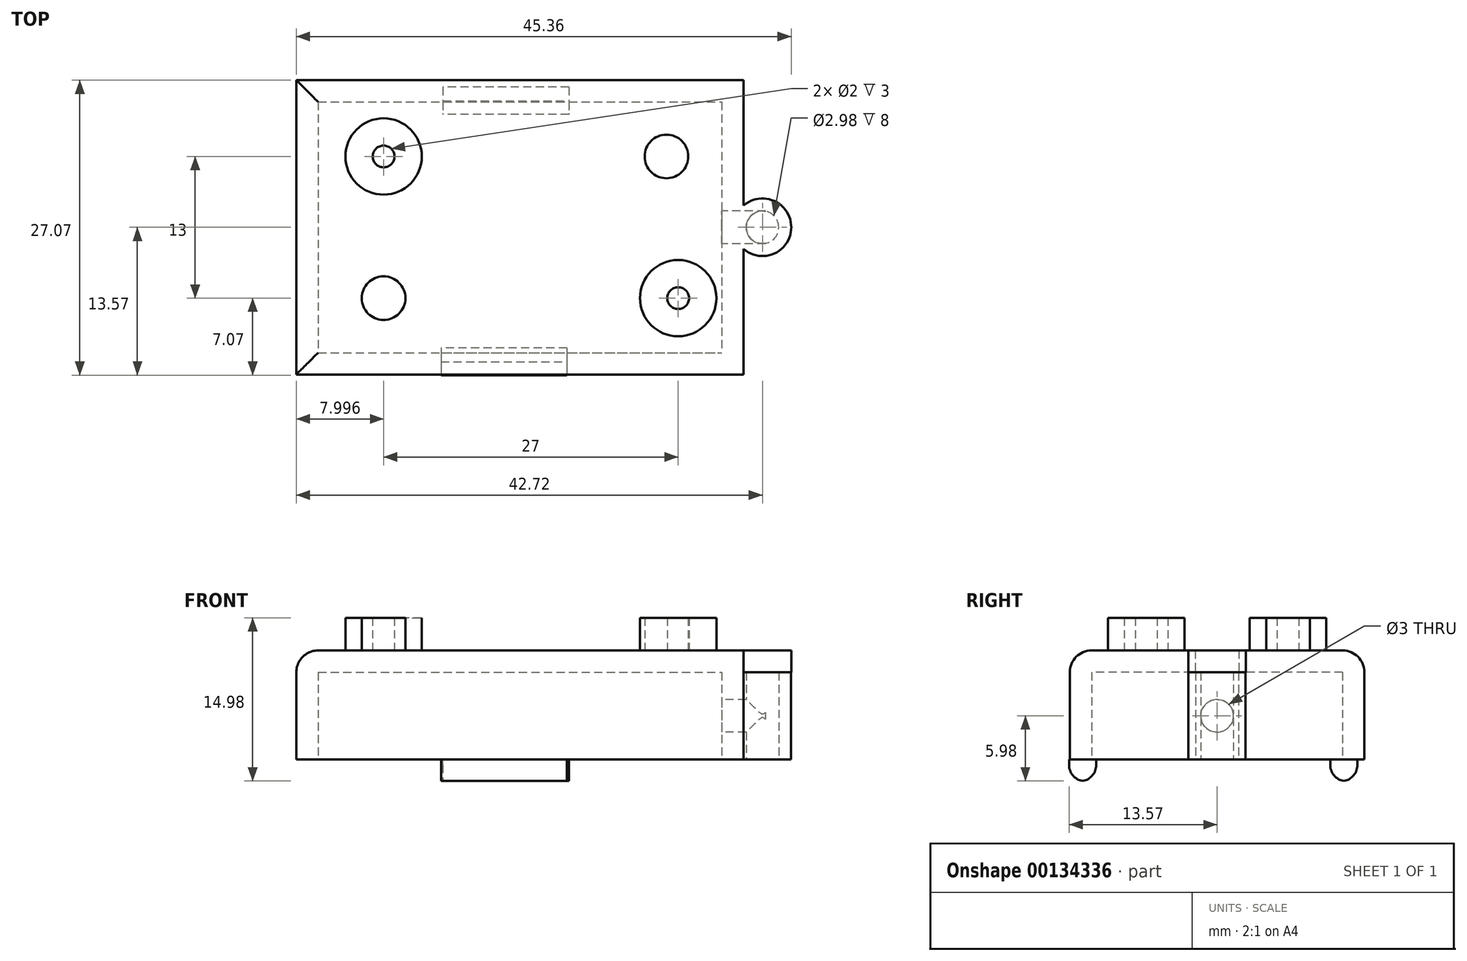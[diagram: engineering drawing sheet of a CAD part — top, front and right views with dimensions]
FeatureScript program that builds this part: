
annotation { "Feature Type Name" : "Feature", "Feature Type Description" : "" }
export const myFeature = defineFeature(function(context is Context, id is Id, definition is map)
    precondition{}
    {
        {
            var Q0;
            Q0=qCreatedBy(makeId("Top.planeOp"),FACE);
            var sketch = newSketch(context, id + "F0", { "sketchPlane" : qUnion([Q0])});
            skLineSegment(sketch, "E0.bottom", {"start": v(-49.4, 25) * mm, "end": v(-12.4, 25) * mm});
            skLineSegment(sketch, "E0.top", {"start": v(-49.4, 2) * mm, "end": v(-12.4, 2) * mm});
            skLineSegment(sketch, "E0.left", {"start": v(-49.4, 25) * mm, "end": v(-49.4, 2) * mm});
            skLineSegment(sketch, "E0.right", {"start": v(-12.4, 25) * mm, "end": v(-12.4, 2) * mm});
            skLineSegment(sketch, "E1.bottom", {"start": v(-51.4, 27) * mm, "end": v(-10.4, 27) * mm});
            skLineSegment(sketch, "E1.top", {"start": v(-51.4, 0) * mm, "end": v(-10.4, 0) * mm});
            skLineSegment(sketch, "E1.left", {"start": v(-51.4, 27) * mm, "end": v(-51.4, 0) * mm});
            skLineSegment(sketch, "E1.right", {"start": v(-10.4, 27) * mm, "end": v(-10.4, 0) * mm});
            skCircle(sketch, "E2", {"center": v(-8.68, 13.5) * mm, "radius": 1.5 * mm});
            skPoint(sketch, "E2.centerSnap0", {"position": v(-10.4, 13.5) * mm});
            skCircle(sketch, "E3", {"center": v(-8.68, 13.5) * mm, "radius": 2.62 * mm});
            skSolve(sketch);
        }
        {
            var Q0;
            Q0=makeQuery(id+"F0.imprint","IMPRINT",FACE,{"disambiguationData":[TD([[makeQuery(id+"F0.imprint","IMPRINT",EDGE,{"derivedFrom":sQuery(id+"F0.wireOp",EDGE,"E0.bottom")}),1.0]])]});
            var Q1;
            Q1=makeQuery(id+"F0.imprint","IMPRINT",FACE,{"disambiguationData":[TD([[makeQuery(id+"F0.imprint","IMPRINT",EDGE,{"derivedFrom":sQuery(id+"F0.wireOp",EDGE,"E2")}),-1.0]])]});
            var Q2;
            {var subQ0=sQuery(id+"F0.wireOp",EDGE,"E3");var subQ1=sQuery(id+"F0.wireOp",EDGE,"E1.right");var subQ2=makeQuery(id+"F0.imprint","INTERSECT",VERTEX,{"disambiguationData":[OD(0.0)],"derivedFrom":[subQ1,subQ0]});Q2=makeQuery(id+"F0.imprint","IMPRINT",FACE,{"disambiguationData":[TD([[makeQuery(id+"F0.imprint","IMPRINT",EDGE,{"disambiguationData":[TD([[subQ2,-1.0]])],"derivedFrom":subQ1}),-1.0]])]});}
            var Q3;
            Q3=sQuery(id+"F0.wireOp",EDGE,"E1.top");
            var Q4;
            Q4=sQuery(id+"F0.wireOp",EDGE,"E1.bottom");
            var Q5;
            Q5=sQuery(id+"F0.wireOp",EDGE,"E0.bottom");
            var Q6;
            Q6=sQuery(id+"F0.wireOp",EDGE,"E1.left");
            var Q7;
            Q7=sQuery(id+"F0.wireOp",EDGE,"E0.left");
            var Q8;
            Q8=sQuery(id+"F0.wireOp",EDGE,"E0.top");
            var Q9;
            Q9=sQuery(id+"F0.wireOp",EDGE,"E0.right");
            var Q10;
            Q10=sQuery(id+"F0.wireOp",EDGE,"E1.right");
            var Q11;
            Q11=sQuery(id+"F0.wireOp",EDGE,"E2");
            var Q12;
            Q12=sQuery(id+"F0.wireOp",EDGE,"E3");
            extrude(context, id + "F1", {"entities" : qUnion([Q0, Q1, Q2]), "surfaceEntities" : qUnion([Q3, Q4, Q5, Q6, Q7, Q8, Q9, Q10, Q11, Q12]), "depth" : 8 * mm});
        }
        {
            var Q0;
            Q0=makeQuery(id+"F1.opExtrude","SWEPT_FACE",FACE,{"disambiguationData":[OSD([sQuery(id+"F0.wireOp",EDGE,"E0.right")])]});
            var sketch = newSketch(context, id + "F2", { "sketchPlane" : qUnion([Q0])});
            skPoint(sketch, "E4", {"position": v(-13.5, 4) * mm});
            skPoint(sketch, "E4.positionSnap0", {"position": v(-13.5, 8) * mm});
            skSolve(sketch);
        }
        {
            var Q0;
            Q0=sQuery(id+"F2.wireOp",VERTEX,"E4");
            var Q1;
            Q1=makeQuery(id+"F1.opExtrude","SWEPT_BODY",BODY,{"disambiguationData":[OSD([sQuery(id+"F0.wireOp",EDGE,"E0.bottom"),sQuery(id+"F0.wireOp",EDGE,"E0.top"),sQuery(id+"F0.wireOp",EDGE,"E0.left"),sQuery(id+"F0.wireOp",EDGE,"E0.right"),sQuery(id+"F0.wireOp",EDGE,"E1.bottom"),sQuery(id+"F0.wireOp",EDGE,"E1.top"),sQuery(id+"F0.wireOp",EDGE,"E1.left"),sQuery(id+"F0.wireOp",EDGE,"E1.right"),sQuery(id+"F0.wireOp",EDGE,"E2"),sQuery(id+"F0.wireOp",EDGE,"E3")])]});
            hole(context, id + "F3", {"style" : HoleStyle.SIMPLE, "endStyle" : HoleEndStyle.BLIND, "holeDiameter" : 3 * mm, "holeDepth" : 4 * mm, "locations" : qUnion([Q0]), "scope" : qUnion([Q1])});
        }
        {
            var Q0;
            Q0=makeQuery(id+"F1.opExtrude","CAP_FACE",FACE,{"disambiguationData":[OSD([sQuery(id+"F0.wireOp",EDGE,"E0.bottom"),sQuery(id+"F0.wireOp",EDGE,"E0.top"),sQuery(id+"F0.wireOp",EDGE,"E0.left"),sQuery(id+"F0.wireOp",EDGE,"E0.right"),sQuery(id+"F0.wireOp",EDGE,"E1.bottom"),sQuery(id+"F0.wireOp",EDGE,"E1.top"),sQuery(id+"F0.wireOp",EDGE,"E1.left"),sQuery(id+"F0.wireOp",EDGE,"E1.right"),sQuery(id+"F0.wireOp",EDGE,"E2"),sQuery(id+"F0.wireOp",EDGE,"E3")])],"isStart":false});
            var sketch = newSketch(context, id + "F4", { "sketchPlane" : qUnion([Q0])});
            skLineSegment(sketch, "E5.bottom", {"start": v(-51.4, 27) * mm, "end": v(-10.4, 27) * mm});
            skLineSegment(sketch, "E5.top", {"start": v(-51.4, 0) * mm, "end": v(-10.4, 0) * mm});
            skLineSegment(sketch, "E5.left", {"start": v(-51.4, 27) * mm, "end": v(-51.4, 0) * mm});
            skLineSegment(sketch, "E5.right", {"start": v(-10.4, 27) * mm, "end": v(-10.4, 0) * mm});
            skCircle(sketch, "E6", {"center": v(-8.68, 13.5) * mm, "radius": 2.64 * mm});
            skSolve(sketch);
        }
        {
            var Q0;
            Q0 = qSketchRegion(id + "F4", true);
            extrude(context, id + "F5", {"entities" : qUnion([Q0]), "operationType" : NewBodyOperationType.ADD, "depth" : 2 * mm});
        }
        {
            var Q0;
            Q0=makeQuery(id+"F5.opExtrude","CAP_EDGE",EDGE,{"disambiguationData":[OSD([sQuery(id+"F4.wireOp",EDGE,"E5.left")])],"isStart":false});
            var Q1;
            Q1=makeQuery(id+"F5.opExtrude","CAP_EDGE",EDGE,{"disambiguationData":[OSD([sQuery(id+"F4.wireOp",EDGE,"E5.bottom")])],"isStart":false});
            var Q2;
            Q2=makeQuery(id+"F5.opExtrude","CAP_EDGE",EDGE,{"disambiguationData":[OSD([sQuery(id+"F4.wireOp",EDGE,"E5.top")])],"isStart":false});
            fillet(context, id + "F6", {"entities" : qUnion([Q0, Q1, Q2]), "radius" : 2 * mm, "tangentPropagation" : true, "allowEdgeOverflow" : false});
        }
        {
            var Q0;
            Q0=qCreatedBy(makeId("Top.planeOp"),FACE);
            var sketch = newSketch(context, id + "F7", { "sketchPlane" : qUnion([Q0])});
            skLineSegment(sketch, "E7.bottom", {"start": v(-26.41, 26.36) * mm, "end": v(-37.96, 26.36) * mm});
            skLineSegment(sketch, "E7.top", {"start": v(-26.41, 23.87) * mm, "end": v(-37.96, 23.87) * mm});
            skLineSegment(sketch, "E7.left", {"start": v(-26.41, 26.36) * mm, "end": v(-26.41, 23.87) * mm});
            skLineSegment(sketch, "E7.right", {"start": v(-37.96, 26.36) * mm, "end": v(-37.96, 23.87) * mm});
            skLineSegment(sketch, "E8.bottom", {"start": v(-26.6, 2.42) * mm, "end": v(-38.14, 2.42) * mm});
            skLineSegment(sketch, "E8.top", {"start": v(-26.6, -0.07) * mm, "end": v(-38.14, -0.07) * mm});
            skLineSegment(sketch, "E8.left", {"start": v(-26.6, 2.42) * mm, "end": v(-26.6, -0.07) * mm});
            skLineSegment(sketch, "E8.right", {"start": v(-38.14, 2.42) * mm, "end": v(-38.14, -0.07) * mm});
            skSolve(sketch);
        }
        {
            var Q0;
            Q0=makeQuery(id+"F7.imprint","IMPRINT",FACE,{"disambiguationData":[TD([[makeQuery(id+"F7.imprint","IMPRINT",EDGE,{"derivedFrom":sQuery(id+"F7.wireOp",EDGE,"E8.bottom")}),1.0]])]});
            var Q1;
            Q1=makeQuery(id+"F7.imprint","IMPRINT",FACE,{"disambiguationData":[TD([[makeQuery(id+"F7.imprint","IMPRINT",EDGE,{"derivedFrom":sQuery(id+"F7.wireOp",EDGE,"E7.bottom")}),1.0]])]});
            extrude(context, id + "F8", {"entities" : qUnion([Q0, Q1]), "operationType" : NewBodyOperationType.ADD, "oppositeDirection" : true, "depth" : 2 * mm});
        }
        {
            var Q0;
            Q0=makeQuery(id+"F8.opExtrude","CAP_EDGE",EDGE,{"disambiguationData":[OSD([sQuery(id+"F7.wireOp",EDGE,"E7.bottom")])],"isStart":false});
            var Q1;
            Q1=makeQuery(id+"F8.opExtrude","CAP_EDGE",EDGE,{"disambiguationData":[OSD([sQuery(id+"F7.wireOp",EDGE,"E7.top")])],"isStart":false});
            fillet(context, id + "F9", {"entities" : qUnion([Q0, Q1]), "radius" : 1.5 * mm, "tangentPropagation" : true, "allowEdgeOverflow" : false});
        }
        {
            var Q0;
            Q0=makeQuery(id+"F8.opExtrude","CAP_EDGE",EDGE,{"disambiguationData":[OSD([sQuery(id+"F7.wireOp",EDGE,"E8.bottom")])],"isStart":false});
            var Q1;
            Q1=makeQuery(id+"F8.opExtrude","CAP_EDGE",EDGE,{"disambiguationData":[OSD([sQuery(id+"F7.wireOp",EDGE,"E8.top")])],"isStart":false});
            fillet(context, id + "F10", {"entities" : qUnion([Q0, Q1]), "radius" : 1.5 * mm, "tangentPropagation" : true, "allowEdgeOverflow" : false});
        }
        {
            var Q0;
            Q0=makeQuery(id+"F5.opExtrude","CAP_FACE",FACE,{"disambiguationData":[OSD([sQuery(id+"F4.wireOp",EDGE,"E5.bottom"),sQuery(id+"F4.wireOp",EDGE,"E5.top"),sQuery(id+"F4.wireOp",EDGE,"E5.left"),sQuery(id+"F4.wireOp",EDGE,"E5.right"),sQuery(id+"F4.wireOp",EDGE,"E6")])],"isStart":false});
            var Q1;
            Q1=makeQuery(id+"F5.opExtrude","CAP_FACE",FACE,{"disambiguationData":[OSD([sQuery(id+"F4.wireOp",EDGE,"E5.bottom"),sQuery(id+"F4.wireOp",EDGE,"E5.top"),sQuery(id+"F4.wireOp",EDGE,"E5.left"),sQuery(id+"F4.wireOp",EDGE,"E5.right"),sQuery(id+"F4.wireOp",EDGE,"E6")])],"isStart":false});
            var sketch = newSketch(context, id + "F11", { "sketchPlane" : qUnion([Q0, Q1])});
            skCircle(sketch, "E9", {"center": v(-16.4, 7) * mm, "radius": 3.5 * mm});
            skCircle(sketch, "E10", {"center": v(-16.4, 7) * mm, "radius": 1 * mm});
            skCircle(sketch, "E11", {"center": v(-43.4, 20) * mm, "radius": 3.5 * mm});
            skCircle(sketch, "E12", {"center": v(-43.4, 20) * mm, "radius": 1 * mm});
            skCircle(sketch, "E13", {"center": v(-43.4, 7) * mm, "radius": 2 * mm});
            skCircle(sketch, "E14", {"center": v(-17.48, 20) * mm, "radius": 2 * mm});
            skSolve(sketch);
        }
        {
            var Q0;
            Q0=makeQuery(id+"F11.imprint","IMPRINT",FACE,{"disambiguationData":[TD([[makeQuery(id+"F11.imprint","IMPRINT",EDGE,{"derivedFrom":sQuery(id+"F11.wireOp",EDGE,"E9")}),1.0]])]});
            var Q1;
            Q1=makeQuery(id+"F11.imprint","IMPRINT",FACE,{"disambiguationData":[TD([[makeQuery(id+"F11.imprint","IMPRINT",EDGE,{"derivedFrom":sQuery(id+"F11.wireOp",EDGE,"E13")}),1.0]])]});
            var Q2;
            Q2=makeQuery(id+"F11.imprint","IMPRINT",FACE,{"disambiguationData":[TD([[makeQuery(id+"F11.imprint","IMPRINT",EDGE,{"derivedFrom":sQuery(id+"F11.wireOp",EDGE,"E11")}),1.0]])]});
            var Q3;
            Q3=makeQuery(id+"F11.imprint","IMPRINT",FACE,{"disambiguationData":[TD([[makeQuery(id+"F11.imprint","IMPRINT",EDGE,{"derivedFrom":sQuery(id+"F11.wireOp",EDGE,"E11")}),1.0]])]});
            var Q4;
            Q4=makeQuery(id+"F11.imprint","IMPRINT",FACE,{"disambiguationData":[TD([[makeQuery(id+"F11.imprint","IMPRINT",EDGE,{"derivedFrom":sQuery(id+"F11.wireOp",EDGE,"E14")}),1.0]])]});
            extrude(context, id + "F12", {"entities" : qUnion([Q0, Q1, Q2, Q3, Q4]), "operationType" : NewBodyOperationType.ADD, "depth" : 3 * mm});
        }
    });
